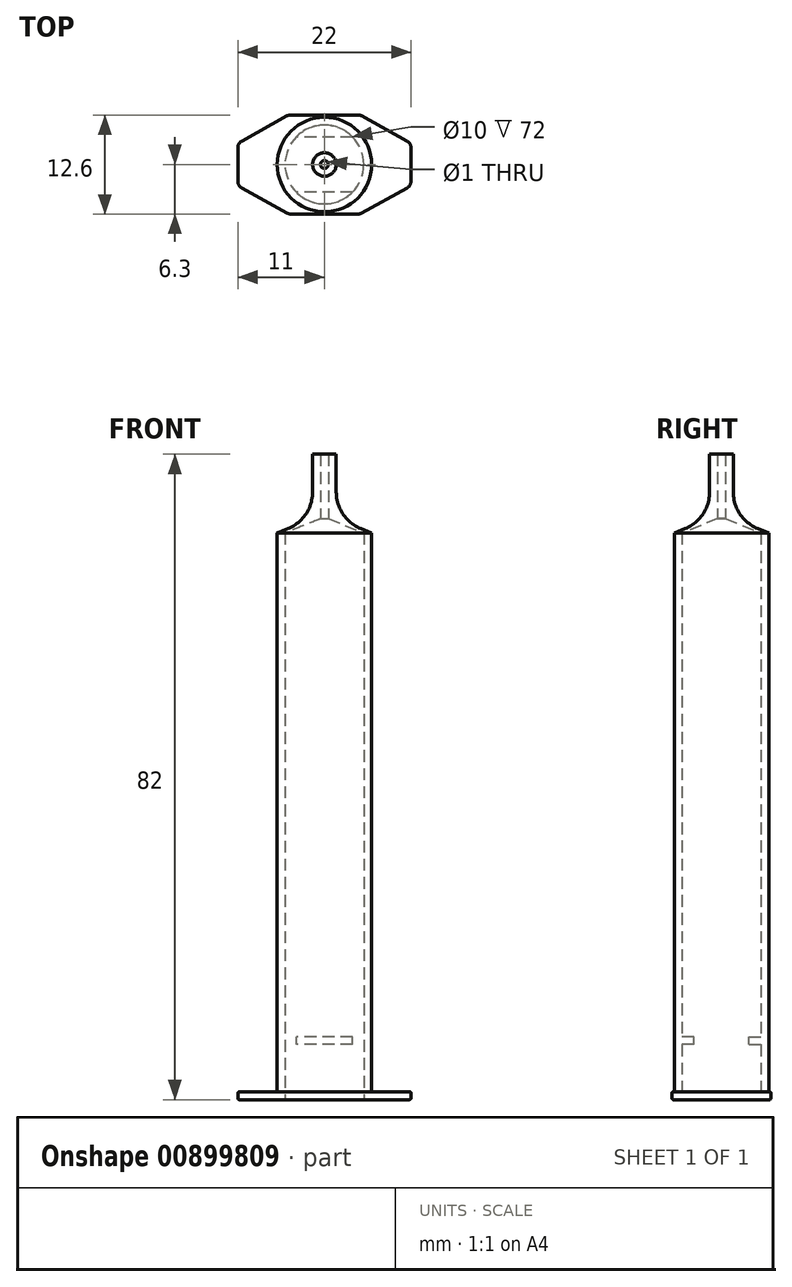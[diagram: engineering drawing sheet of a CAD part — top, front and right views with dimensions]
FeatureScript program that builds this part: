
annotation { "Feature Type Name" : "Feature", "Feature Type Description" : "" }
export const myFeature = defineFeature(function(context is Context, id is Id, definition is map)
    precondition{}
    {
        {
            var Q0;
            Q0=qCreatedBy(makeId("Top.planeOp"),FACE);
            var sketch = newSketch(context, id + "F0", { "sketchPlane" : qUnion([Q0])});
            skCircle(sketch, "E0", {"center": v(0, 0) * mm, "radius": 5 * mm});
            skCircle(sketch, "E1", {"center": v(0, 0) * mm, "radius": 6 * mm});
            skSolve(sketch);
        }
        {
            var Q0;
            Q0=makeQuery(id+"F0.imprint","IMPRINT",FACE,{"disambiguationData":[TD([[makeQuery(id+"F0.imprint","IMPRINT",EDGE,{"derivedFrom":sQuery(id+"F0.wireOp",EDGE,"E0")}),-1.0]])]});
            extrude(context, id + "F1", {"entities" : qUnion([Q0]), "depth" : 62 * mm, "offsetDistance" : 25 * mm, "hasSecondDirection" : true, "secondDirectionOppositeDirection" : true, "secondDirectionDepth" : 9 * mm});
        }
        {
            var Q0;
            Q0=qCreatedBy(makeId("Front.planeOp"),FACE);
            var sketch = newSketch(context, id + "F2", { "sketchPlane" : qUnion([Q0])});
            skLineSegment(sketch, "E2", {"start": v(4.64, 62.54) * mm, "end": v(6, 62) * mm});
            skLineSegment(sketch, "E3", {"start": v(0, 62) * mm, "end": v(6, 62) * mm});
            skLineSegment(sketch, "E4", {"start": v(0.5, 63.8) * mm, "end": v(5, 62) * mm});
            skLineSegment(sketch, "E5", {"start": v(0.5, 63.8) * mm, "end": v(0.5, 72) * mm});
            skLineSegment(sketch, "E6", {"start": v(1.5, 67.19) * mm, "end": v(1.5, 72) * mm});
            skLineSegment(sketch, "E7", {"start": v(0.5, 72) * mm, "end": v(1.5, 72) * mm});
            skLineSegment(sketch, "E8", {"start": v(0, 62) * mm, "end": v(0, 62.89) * mm});
            skPoint(sketch, "E9.visualSharp", {"position": v(1.5, 63.8) * mm});
            skArc(sketch, "E9.filletArc", {"start": v(1.5, 67.19) * mm, "mid": v(2.36, 64.38) * mm, "end": v(4.64, 62.54) * mm});
            skSolve(sketch);
        }
        {
            var Q0;
            {var subQ2=sQuery(id+"F2.wireOp",EDGE,"E2");Q0=makeQuery(id+"F2.imprint","IMPRINT",FACE,{"disambiguationData":[TD([[makeQuery(id+"F2.imprint","IMPRINT",EDGE,{"derivedFrom":subQ2}),-1.0]])]});}
            var Q1;
            Q1=sQuery(id+"F2.wireOp",EDGE,"E8");
            revolve(context, id + "F3", {"operationType" : NewBodyOperationType.ADD, "surfaceOperationType" : NewSurfaceOperationType.NEW, "entities" : qUnion([Q0]), "axis" : qUnion([Q1]), "revolveType" : RevolveType.FULL});
        }
        {
            var Q0;
            Q0=makeQuery(id+"F3.opRevolve","SWEPT_FACE",FACE,{"disambiguationData":[OSD([sQuery(id+"F2.wireOp",EDGE,"E7")])]});
            cPlane(context, id + "F4", {"entities" : qUnion([Q0]), "cplaneType" : CPlaneType.OFFSET, "offset" : 74 * mm, "oppositeDirection" : true, "width" : 150 * mm, "height" : 150 * mm});
        }
        {
            var Q0;
            Q0=qCreatedBy(id+"F4.planeOp",FACE);
            var sketch = newSketch(context, id + "F5", { "sketchPlane" : qUnion([Q0])});
            skLineSegment(sketch, "E10", {"start": v(3.57, 3.5) * mm, "end": v(-3.57, 3.5) * mm});
            skLineSegment(sketch, "E11.MirrorCS", {"start": v(3.57, -3.5) * mm, "end": v(-3.57, -3.5) * mm});
            skArc(sketch, "E12", {"start": v(-3.57, -3.5) * mm, "mid": v(0, -5) * mm, "end": v(3.57, -3.5) * mm});
            skArc(sketch, "E13.MirrorCS", {"start": v(-3.57, 3.5) * mm, "mid": v(0, 5) * mm, "end": v(3.57, 3.5) * mm});
            skSolve(sketch);
        }
        {
            var Q0;
            Q0=makeQuery(id+"F5.imprint","IMPRINT",FACE,{"disambiguationData":[TD([[makeQuery(id+"F5.imprint","IMPRINT",EDGE,{"derivedFrom":sQuery(id+"F5.wireOp",EDGE,"E11.MirrorCS")}),1.0]])]});
            var Q1;
            Q1=makeQuery(id+"F5.imprint","IMPRINT",FACE,{"disambiguationData":[TD([[makeQuery(id+"F5.imprint","IMPRINT",EDGE,{"derivedFrom":sQuery(id+"F5.wireOp",EDGE,"E10")}),-1.0]])]});
            extrude(context, id + "F6", {"entities" : qUnion([Q0, Q1]), "operationType" : NewBodyOperationType.ADD, "oppositeDirection" : true, "depth" : 1 * mm, "offsetDistance" : 25 * mm});
        }
        {
            var Q0;
            Q0=makeQuery(id+"F1.opExtrude","CAP_FACE",FACE,{"disambiguationData":[OSD([sQuery(id+"F0.wireOp",EDGE,"E0"),sQuery(id+"F0.wireOp",EDGE,"E1")])],"isStart":true});
            cPlane(context, id + "F7", {"entities" : qUnion([Q0]), "cplaneType" : CPlaneType.OFFSET, "offset" : 0 * mm, "width" : 150 * mm, "height" : 150 * mm});
        }
        {
            var Q0;
            Q0=qCreatedBy(id+"F7.planeOp",FACE);
            var sketch = newSketch(context, id + "F8", { "sketchPlane" : qUnion([Q0])});
            skLineSegment(sketch, "E14", {"start": v(4.5, 6.3) * mm, "end": v(11, 2.71) * mm});
            skLineSegment(sketch, "E15.MirrorCS", {"start": v(4.5, -6.3) * mm, "end": v(11, -2.71) * mm});
            skLineSegment(sketch, "E16.MirrorCS", {"start": v(-4.5, 6.3) * mm, "end": v(-11, 2.71) * mm});
            skLineSegment(sketch, "E17.MirrorCS", {"start": v(-4.5, -6.3) * mm, "end": v(-11, -2.71) * mm});
            skCircle(sketch, "E18", {"center": v(0, 0) * mm, "radius": 5 * mm});
            skLineSegment(sketch, "E19", {"start": v(4.5, 6.3) * mm, "end": v(-4.5, 6.3) * mm});
            skLineSegment(sketch, "E20", {"start": v(4.5, -6.3) * mm, "end": v(-4.5, -6.3) * mm});
            skLineSegment(sketch, "E21", {"start": v(11, 2.71) * mm, "end": v(11, -2.71) * mm});
            skLineSegment(sketch, "E22", {"start": v(-11, 2.71) * mm, "end": v(-11, -2.71) * mm});
            skSolve(sketch);
        }
        {
            var Q0;
            Q0=makeQuery(id+"F8.imprint","IMPRINT",FACE,{"disambiguationData":[TD([[makeQuery(id+"F8.imprint","IMPRINT",EDGE,{"derivedFrom":sQuery(id+"F8.wireOp",EDGE,"Z6K4M87V-DVPl-VIz8-pgWM-HxpkCWdUFoVx.top")}),1.0]])]});
            var Q1;
            Q1=makeQuery(id+"F8.imprint","IMPRINT",FACE,{"disambiguationData":[TD([[makeQuery(id+"F8.imprint","IMPRINT",EDGE,{"derivedFrom":sQuery(id+"F8.wireOp",EDGE,"E14")}),-1.0]])]});
            extrude(context, id + "F9", {"entities" : qUnion([Q0, Q1]), "operationType" : NewBodyOperationType.ADD, "depth" : 1 * mm, "offsetDistance" : 25 * mm});
        }
        {
            var Q0;
            Q0=makeQuery(id+"F9.opExtrude","SWEPT_EDGE",EDGE,{"disambiguationData":[OSD([sQuery(id+"F8.wireOp",EDGE,"df01a680-1bff-42a6-ba12-da2397d9a9860.MirrorCS"),sQuery(id+"F8.wireOp",EDGE,"E16.MirrorCS")])]});
            var Q1;
            Q1=makeQuery(id+"F9.opExtrude","SWEPT_EDGE",EDGE,{"disambiguationData":[OSD([sQuery(id+"F8.wireOp",EDGE,"07e45aba-89c8-4687-9971-865d9c13b24f0.MirrorCS"),sQuery(id+"F8.wireOp",EDGE,"E17.MirrorCS")])]});
            var Q2;
            Q2=makeQuery(id+"F9.opExtrude","SWEPT_EDGE",EDGE,{"disambiguationData":[OSD([sQuery(id+"F8.wireOp",EDGE,"Z6K4M87V-DVPl-VIz8-pgWM-HxpkCWdUFoVx.right"),sQuery(id+"F8.wireOp",EDGE,"E15.MirrorCS")])]});
            var Q3;
            Q3=makeQuery(id+"F9.opExtrude","SWEPT_EDGE",EDGE,{"disambiguationData":[OSD([sQuery(id+"F8.wireOp",EDGE,"6886a79b-2828-4634-8f31-eee592987a7b0.MirrorCS"),sQuery(id+"F8.wireOp",EDGE,"E14")])]});
            fillet(context, id + "F10", {"entities" : qUnion([Q0, Q1, Q2, Q3]), "radius" : 1 * mm, "tangentPropagation" : true, "allowEdgeOverflow" : false});
        }
        {
            var Q0;
            Q0=makeQuery(id+"F9.opExtrude","CAP_EDGE",EDGE,{"disambiguationData":[OSD([sQuery(id+"F8.wireOp",EDGE,"E16.MirrorCS")])],"isStart":false});
            var Q1;
            {var subQ0=sQuery(id+"F8.wireOp",EDGE,"E19");var subQ1=sQuery(id+"F8.wireOp",EDGE,"E16.MirrorCS");Q1=makeQuery(id+"F10.opFillet","BLEND_EDGE",EDGE,{"blendedFrom":[makeQuery(id+"F9.opExtrude","SWEPT_EDGE",EDGE,{"disambiguationData":[OSD([subQ1,subQ0])]}),makeQuery(id+"F9.opExtrude","CAP_FACE",FACE,{"disambiguationData":[OSD([sQuery(id+"F8.wireOp",EDGE,"E14"),sQuery(id+"F8.wireOp",EDGE,"E15.MirrorCS"),subQ1,sQuery(id+"F8.wireOp",EDGE,"E17.MirrorCS"),sQuery(id+"F8.wireOp",EDGE,"E18"),subQ0,sQuery(id+"F8.wireOp",EDGE,"E20"),sQuery(id+"F8.wireOp",EDGE,"E21"),sQuery(id+"F8.wireOp",EDGE,"E22")])],"isStart":false})],"blendedInto":[makeQuery(id+"F9.opExtrude","CAP_FACE",FACE,{"disambiguationData":[OSD([sQuery(id+"F8.wireOp",EDGE,"E14"),sQuery(id+"F8.wireOp",EDGE,"E15.MirrorCS"),subQ1,sQuery(id+"F8.wireOp",EDGE,"E17.MirrorCS"),sQuery(id+"F8.wireOp",EDGE,"E18"),subQ0,sQuery(id+"F8.wireOp",EDGE,"E20"),sQuery(id+"F8.wireOp",EDGE,"E21"),sQuery(id+"F8.wireOp",EDGE,"E22")])],"isStart":false})]});}
            var Q2;
            Q2=makeQuery(id+"F9.opExtrude","CAP_EDGE",EDGE,{"disambiguationData":[OSD([sQuery(id+"F8.wireOp",EDGE,"E19")])],"isStart":false});
            var Q3;
            Q3=makeQuery(id+"F9.opExtrude","CAP_EDGE",EDGE,{"disambiguationData":[OSD([sQuery(id+"F8.wireOp",EDGE,"E22")])],"isStart":false});
            var Q4;
            {var subQ0=sQuery(id+"F8.wireOp",EDGE,"E22");var subQ1=sQuery(id+"F8.wireOp",EDGE,"E16.MirrorCS");Q4=makeQuery(id+"F10.opFillet","BLEND_EDGE",EDGE,{"blendedFrom":[makeQuery(id+"F9.opExtrude","SWEPT_EDGE",EDGE,{"disambiguationData":[OSD([subQ1,subQ0])]}),makeQuery(id+"F9.opExtrude","CAP_FACE",FACE,{"disambiguationData":[OSD([sQuery(id+"F8.wireOp",EDGE,"E14"),sQuery(id+"F8.wireOp",EDGE,"E15.MirrorCS"),subQ1,sQuery(id+"F8.wireOp",EDGE,"E17.MirrorCS"),sQuery(id+"F8.wireOp",EDGE,"E18"),sQuery(id+"F8.wireOp",EDGE,"E19"),sQuery(id+"F8.wireOp",EDGE,"E20"),sQuery(id+"F8.wireOp",EDGE,"E21"),subQ0])],"isStart":false})],"blendedInto":[makeQuery(id+"F9.opExtrude","CAP_FACE",FACE,{"disambiguationData":[OSD([sQuery(id+"F8.wireOp",EDGE,"E14"),sQuery(id+"F8.wireOp",EDGE,"E15.MirrorCS"),subQ1,sQuery(id+"F8.wireOp",EDGE,"E17.MirrorCS"),sQuery(id+"F8.wireOp",EDGE,"E18"),sQuery(id+"F8.wireOp",EDGE,"E19"),sQuery(id+"F8.wireOp",EDGE,"E20"),sQuery(id+"F8.wireOp",EDGE,"E21"),subQ0])],"isStart":false})]});}
            var Q5;
            {var subQ0=sQuery(id+"F8.wireOp",EDGE,"E22");var subQ1=sQuery(id+"F8.wireOp",EDGE,"E17.MirrorCS");Q5=makeQuery(id+"F10.opFillet","BLEND_EDGE",EDGE,{"blendedFrom":[makeQuery(id+"F9.opExtrude","SWEPT_EDGE",EDGE,{"disambiguationData":[OSD([subQ1,subQ0])]}),makeQuery(id+"F9.opExtrude","CAP_FACE",FACE,{"disambiguationData":[OSD([sQuery(id+"F8.wireOp",EDGE,"E14"),sQuery(id+"F8.wireOp",EDGE,"E15.MirrorCS"),sQuery(id+"F8.wireOp",EDGE,"E16.MirrorCS"),subQ1,sQuery(id+"F8.wireOp",EDGE,"E18"),sQuery(id+"F8.wireOp",EDGE,"E19"),sQuery(id+"F8.wireOp",EDGE,"E20"),sQuery(id+"F8.wireOp",EDGE,"E21"),subQ0])],"isStart":false})],"blendedInto":[makeQuery(id+"F9.opExtrude","CAP_FACE",FACE,{"disambiguationData":[OSD([sQuery(id+"F8.wireOp",EDGE,"E14"),sQuery(id+"F8.wireOp",EDGE,"E15.MirrorCS"),sQuery(id+"F8.wireOp",EDGE,"E16.MirrorCS"),subQ1,sQuery(id+"F8.wireOp",EDGE,"E18"),sQuery(id+"F8.wireOp",EDGE,"E19"),sQuery(id+"F8.wireOp",EDGE,"E20"),sQuery(id+"F8.wireOp",EDGE,"E21"),subQ0])],"isStart":false})]});}
            var Q6;
            Q6=makeQuery(id+"F9.opExtrude","CAP_EDGE",EDGE,{"disambiguationData":[OSD([sQuery(id+"F8.wireOp",EDGE,"E17.MirrorCS")])],"isStart":false});
            var Q7;
            {var subQ0=sQuery(id+"F8.wireOp",EDGE,"E20");var subQ1=sQuery(id+"F8.wireOp",EDGE,"E17.MirrorCS");Q7=makeQuery(id+"F10.opFillet","BLEND_EDGE",EDGE,{"blendedFrom":[makeQuery(id+"F9.opExtrude","SWEPT_EDGE",EDGE,{"disambiguationData":[OSD([subQ1,subQ0])]}),makeQuery(id+"F9.opExtrude","CAP_FACE",FACE,{"disambiguationData":[OSD([sQuery(id+"F8.wireOp",EDGE,"E14"),sQuery(id+"F8.wireOp",EDGE,"E15.MirrorCS"),sQuery(id+"F8.wireOp",EDGE,"E16.MirrorCS"),subQ1,sQuery(id+"F8.wireOp",EDGE,"E18"),sQuery(id+"F8.wireOp",EDGE,"E19"),subQ0,sQuery(id+"F8.wireOp",EDGE,"E21"),sQuery(id+"F8.wireOp",EDGE,"E22")])],"isStart":false})],"blendedInto":[makeQuery(id+"F9.opExtrude","CAP_FACE",FACE,{"disambiguationData":[OSD([sQuery(id+"F8.wireOp",EDGE,"E14"),sQuery(id+"F8.wireOp",EDGE,"E15.MirrorCS"),sQuery(id+"F8.wireOp",EDGE,"E16.MirrorCS"),subQ1,sQuery(id+"F8.wireOp",EDGE,"E18"),sQuery(id+"F8.wireOp",EDGE,"E19"),subQ0,sQuery(id+"F8.wireOp",EDGE,"E21"),sQuery(id+"F8.wireOp",EDGE,"E22")])],"isStart":false})]});}
            var Q8;
            Q8=makeQuery(id+"F9.opExtrude","CAP_EDGE",EDGE,{"disambiguationData":[OSD([sQuery(id+"F8.wireOp",EDGE,"E20")])],"isStart":false});
            var Q9;
            {var subQ0=sQuery(id+"F8.wireOp",EDGE,"E20");var subQ1=sQuery(id+"F8.wireOp",EDGE,"E15.MirrorCS");Q9=makeQuery(id+"F10.opFillet","BLEND_EDGE",EDGE,{"blendedFrom":[makeQuery(id+"F9.opExtrude","SWEPT_EDGE",EDGE,{"disambiguationData":[OSD([subQ1,subQ0])]}),makeQuery(id+"F9.opExtrude","CAP_FACE",FACE,{"disambiguationData":[OSD([sQuery(id+"F8.wireOp",EDGE,"E14"),subQ1,sQuery(id+"F8.wireOp",EDGE,"E16.MirrorCS"),sQuery(id+"F8.wireOp",EDGE,"E17.MirrorCS"),sQuery(id+"F8.wireOp",EDGE,"E18"),sQuery(id+"F8.wireOp",EDGE,"E19"),subQ0,sQuery(id+"F8.wireOp",EDGE,"E21"),sQuery(id+"F8.wireOp",EDGE,"E22")])],"isStart":false})],"blendedInto":[makeQuery(id+"F9.opExtrude","CAP_FACE",FACE,{"disambiguationData":[OSD([sQuery(id+"F8.wireOp",EDGE,"E14"),subQ1,sQuery(id+"F8.wireOp",EDGE,"E16.MirrorCS"),sQuery(id+"F8.wireOp",EDGE,"E17.MirrorCS"),sQuery(id+"F8.wireOp",EDGE,"E18"),sQuery(id+"F8.wireOp",EDGE,"E19"),subQ0,sQuery(id+"F8.wireOp",EDGE,"E21"),sQuery(id+"F8.wireOp",EDGE,"E22")])],"isStart":false})]});}
            var Q10;
            Q10=makeQuery(id+"F9.opExtrude","CAP_EDGE",EDGE,{"disambiguationData":[OSD([sQuery(id+"F8.wireOp",EDGE,"E15.MirrorCS")])],"isStart":false});
            var Q11;
            Q11=makeQuery(id+"F9.opExtrude","CAP_EDGE",EDGE,{"disambiguationData":[OSD([sQuery(id+"F8.wireOp",EDGE,"E14")])],"isStart":false});
            var Q12;
            {var subQ0=sQuery(id+"F8.wireOp",EDGE,"E19");var subQ1=sQuery(id+"F8.wireOp",EDGE,"E14");Q12=makeQuery(id+"F10.opFillet","BLEND_EDGE",EDGE,{"blendedFrom":[makeQuery(id+"F9.opExtrude","SWEPT_EDGE",EDGE,{"disambiguationData":[OSD([subQ1,subQ0])]}),makeQuery(id+"F9.opExtrude","CAP_FACE",FACE,{"disambiguationData":[OSD([subQ1,sQuery(id+"F8.wireOp",EDGE,"E15.MirrorCS"),sQuery(id+"F8.wireOp",EDGE,"E16.MirrorCS"),sQuery(id+"F8.wireOp",EDGE,"E17.MirrorCS"),sQuery(id+"F8.wireOp",EDGE,"E18"),subQ0,sQuery(id+"F8.wireOp",EDGE,"E20"),sQuery(id+"F8.wireOp",EDGE,"E21"),sQuery(id+"F8.wireOp",EDGE,"E22")])],"isStart":false})],"blendedInto":[makeQuery(id+"F9.opExtrude","CAP_FACE",FACE,{"disambiguationData":[OSD([subQ1,sQuery(id+"F8.wireOp",EDGE,"E15.MirrorCS"),sQuery(id+"F8.wireOp",EDGE,"E16.MirrorCS"),sQuery(id+"F8.wireOp",EDGE,"E17.MirrorCS"),sQuery(id+"F8.wireOp",EDGE,"E18"),subQ0,sQuery(id+"F8.wireOp",EDGE,"E20"),sQuery(id+"F8.wireOp",EDGE,"E21"),sQuery(id+"F8.wireOp",EDGE,"E22")])],"isStart":false})]});}
            var Q13;
            {var subQ0=sQuery(id+"F8.wireOp",EDGE,"E21");var subQ1=sQuery(id+"F8.wireOp",EDGE,"E14");Q13=makeQuery(id+"F10.opFillet","BLEND_EDGE",EDGE,{"blendedFrom":[makeQuery(id+"F9.opExtrude","SWEPT_EDGE",EDGE,{"disambiguationData":[OSD([subQ1,subQ0])]}),makeQuery(id+"F9.opExtrude","CAP_FACE",FACE,{"disambiguationData":[OSD([subQ1,sQuery(id+"F8.wireOp",EDGE,"E15.MirrorCS"),sQuery(id+"F8.wireOp",EDGE,"E16.MirrorCS"),sQuery(id+"F8.wireOp",EDGE,"E17.MirrorCS"),sQuery(id+"F8.wireOp",EDGE,"E18"),sQuery(id+"F8.wireOp",EDGE,"E19"),sQuery(id+"F8.wireOp",EDGE,"E20"),subQ0,sQuery(id+"F8.wireOp",EDGE,"E22")])],"isStart":false})],"blendedInto":[makeQuery(id+"F9.opExtrude","CAP_FACE",FACE,{"disambiguationData":[OSD([subQ1,sQuery(id+"F8.wireOp",EDGE,"E15.MirrorCS"),sQuery(id+"F8.wireOp",EDGE,"E16.MirrorCS"),sQuery(id+"F8.wireOp",EDGE,"E17.MirrorCS"),sQuery(id+"F8.wireOp",EDGE,"E18"),sQuery(id+"F8.wireOp",EDGE,"E19"),sQuery(id+"F8.wireOp",EDGE,"E20"),subQ0,sQuery(id+"F8.wireOp",EDGE,"E22")])],"isStart":false})]});}
            var Q14;
            Q14=makeQuery(id+"F9.opExtrude","CAP_EDGE",EDGE,{"disambiguationData":[OSD([sQuery(id+"F8.wireOp",EDGE,"E21")])],"isStart":false});
            var Q15;
            {var subQ0=sQuery(id+"F8.wireOp",EDGE,"E21");var subQ1=sQuery(id+"F8.wireOp",EDGE,"E15.MirrorCS");Q15=makeQuery(id+"F10.opFillet","BLEND_EDGE",EDGE,{"blendedFrom":[makeQuery(id+"F9.opExtrude","SWEPT_EDGE",EDGE,{"disambiguationData":[OSD([subQ1,subQ0])]}),makeQuery(id+"F9.opExtrude","CAP_FACE",FACE,{"disambiguationData":[OSD([sQuery(id+"F8.wireOp",EDGE,"E14"),subQ1,sQuery(id+"F8.wireOp",EDGE,"E16.MirrorCS"),sQuery(id+"F8.wireOp",EDGE,"E17.MirrorCS"),sQuery(id+"F8.wireOp",EDGE,"E18"),sQuery(id+"F8.wireOp",EDGE,"E19"),sQuery(id+"F8.wireOp",EDGE,"E20"),subQ0,sQuery(id+"F8.wireOp",EDGE,"E22")])],"isStart":false})],"blendedInto":[makeQuery(id+"F9.opExtrude","CAP_FACE",FACE,{"disambiguationData":[OSD([sQuery(id+"F8.wireOp",EDGE,"E14"),subQ1,sQuery(id+"F8.wireOp",EDGE,"E16.MirrorCS"),sQuery(id+"F8.wireOp",EDGE,"E17.MirrorCS"),sQuery(id+"F8.wireOp",EDGE,"E18"),sQuery(id+"F8.wireOp",EDGE,"E19"),sQuery(id+"F8.wireOp",EDGE,"E20"),subQ0,sQuery(id+"F8.wireOp",EDGE,"E22")])],"isStart":false})]});}
            fillet(context, id + "F11", {"entities" : qUnion([Q0, Q1, Q2, Q3, Q4, Q5, Q6, Q7, Q8, Q9, Q10, Q11, Q12, Q13, Q14, Q15]), "radius" : .2 * mm, "tangentPropagation" : true, "allowEdgeOverflow" : false});
        }
        {
            var Q0;
            {var subQ0=sQuery(id+"F8.wireOp",EDGE,"E21");var subQ1=sQuery(id+"F8.wireOp",EDGE,"E14");Q0=makeQuery(id+"F10.opFillet","BLEND_EDGE",EDGE,{"blendedFrom":[makeQuery(id+"F9.opExtrude","SWEPT_EDGE",EDGE,{"disambiguationData":[OSD([subQ1,subQ0])]}),makeQuery(id+"F9.opExtrude","CAP_FACE",FACE,{"disambiguationData":[OSD([subQ1,sQuery(id+"F8.wireOp",EDGE,"E15.MirrorCS"),sQuery(id+"F8.wireOp",EDGE,"E16.MirrorCS"),sQuery(id+"F8.wireOp",EDGE,"E17.MirrorCS"),sQuery(id+"F8.wireOp",EDGE,"E18"),sQuery(id+"F8.wireOp",EDGE,"E19"),sQuery(id+"F8.wireOp",EDGE,"E20"),subQ0,sQuery(id+"F8.wireOp",EDGE,"E22")])],"isStart":true})],"blendedInto":[makeQuery(id+"F9.opExtrude","CAP_FACE",FACE,{"disambiguationData":[OSD([subQ1,sQuery(id+"F8.wireOp",EDGE,"E15.MirrorCS"),sQuery(id+"F8.wireOp",EDGE,"E16.MirrorCS"),sQuery(id+"F8.wireOp",EDGE,"E17.MirrorCS"),sQuery(id+"F8.wireOp",EDGE,"E18"),sQuery(id+"F8.wireOp",EDGE,"E19"),sQuery(id+"F8.wireOp",EDGE,"E20"),subQ0,sQuery(id+"F8.wireOp",EDGE,"E22")])],"isStart":true})]});}
            var Q1;
            Q1=makeQuery(id+"F9.opExtrude","CAP_EDGE",EDGE,{"disambiguationData":[OSD([sQuery(id+"F8.wireOp",EDGE,"E21")])],"isStart":true});
            var Q2;
            {var subQ0=sQuery(id+"F8.wireOp",EDGE,"E21");var subQ1=sQuery(id+"F8.wireOp",EDGE,"E15.MirrorCS");Q2=makeQuery(id+"F10.opFillet","BLEND_EDGE",EDGE,{"blendedFrom":[makeQuery(id+"F9.opExtrude","SWEPT_EDGE",EDGE,{"disambiguationData":[OSD([subQ1,subQ0])]}),makeQuery(id+"F9.opExtrude","CAP_FACE",FACE,{"disambiguationData":[OSD([sQuery(id+"F8.wireOp",EDGE,"E14"),subQ1,sQuery(id+"F8.wireOp",EDGE,"E16.MirrorCS"),sQuery(id+"F8.wireOp",EDGE,"E17.MirrorCS"),sQuery(id+"F8.wireOp",EDGE,"E18"),sQuery(id+"F8.wireOp",EDGE,"E19"),sQuery(id+"F8.wireOp",EDGE,"E20"),subQ0,sQuery(id+"F8.wireOp",EDGE,"E22")])],"isStart":true})],"blendedInto":[makeQuery(id+"F9.opExtrude","CAP_FACE",FACE,{"disambiguationData":[OSD([sQuery(id+"F8.wireOp",EDGE,"E14"),subQ1,sQuery(id+"F8.wireOp",EDGE,"E16.MirrorCS"),sQuery(id+"F8.wireOp",EDGE,"E17.MirrorCS"),sQuery(id+"F8.wireOp",EDGE,"E18"),sQuery(id+"F8.wireOp",EDGE,"E19"),sQuery(id+"F8.wireOp",EDGE,"E20"),subQ0,sQuery(id+"F8.wireOp",EDGE,"E22")])],"isStart":true})]});}
            var Q3;
            Q3=makeQuery(id+"F9.opExtrude","CAP_EDGE",EDGE,{"disambiguationData":[OSD([sQuery(id+"F8.wireOp",EDGE,"E15.MirrorCS")])],"isStart":true});
            var Q4;
            {var subQ0=sQuery(id+"F8.wireOp",EDGE,"E20");var subQ1=sQuery(id+"F8.wireOp",EDGE,"E15.MirrorCS");Q4=makeQuery(id+"F10.opFillet","BLEND_EDGE",EDGE,{"blendedFrom":[makeQuery(id+"F9.opExtrude","SWEPT_EDGE",EDGE,{"disambiguationData":[OSD([subQ1,subQ0])]}),makeQuery(id+"F9.opExtrude","CAP_FACE",FACE,{"disambiguationData":[OSD([sQuery(id+"F8.wireOp",EDGE,"E14"),subQ1,sQuery(id+"F8.wireOp",EDGE,"E16.MirrorCS"),sQuery(id+"F8.wireOp",EDGE,"E17.MirrorCS"),sQuery(id+"F8.wireOp",EDGE,"E18"),sQuery(id+"F8.wireOp",EDGE,"E19"),subQ0,sQuery(id+"F8.wireOp",EDGE,"E21"),sQuery(id+"F8.wireOp",EDGE,"E22")])],"isStart":true})],"blendedInto":[makeQuery(id+"F9.opExtrude","CAP_FACE",FACE,{"disambiguationData":[OSD([sQuery(id+"F8.wireOp",EDGE,"E14"),subQ1,sQuery(id+"F8.wireOp",EDGE,"E16.MirrorCS"),sQuery(id+"F8.wireOp",EDGE,"E17.MirrorCS"),sQuery(id+"F8.wireOp",EDGE,"E18"),sQuery(id+"F8.wireOp",EDGE,"E19"),subQ0,sQuery(id+"F8.wireOp",EDGE,"E21"),sQuery(id+"F8.wireOp",EDGE,"E22")])],"isStart":true})]});}
            var Q5;
            Q5=makeQuery(id+"F9.opExtrude","CAP_EDGE",EDGE,{"disambiguationData":[OSD([sQuery(id+"F8.wireOp",EDGE,"E20")])],"isStart":true});
            var Q6;
            {var subQ0=sQuery(id+"F8.wireOp",EDGE,"E20");var subQ1=sQuery(id+"F8.wireOp",EDGE,"E17.MirrorCS");Q6=makeQuery(id+"F10.opFillet","BLEND_EDGE",EDGE,{"blendedFrom":[makeQuery(id+"F9.opExtrude","SWEPT_EDGE",EDGE,{"disambiguationData":[OSD([subQ1,subQ0])]}),makeQuery(id+"F9.opExtrude","CAP_FACE",FACE,{"disambiguationData":[OSD([sQuery(id+"F8.wireOp",EDGE,"E14"),sQuery(id+"F8.wireOp",EDGE,"E15.MirrorCS"),sQuery(id+"F8.wireOp",EDGE,"E16.MirrorCS"),subQ1,sQuery(id+"F8.wireOp",EDGE,"E18"),sQuery(id+"F8.wireOp",EDGE,"E19"),subQ0,sQuery(id+"F8.wireOp",EDGE,"E21"),sQuery(id+"F8.wireOp",EDGE,"E22")])],"isStart":true})],"blendedInto":[makeQuery(id+"F9.opExtrude","CAP_FACE",FACE,{"disambiguationData":[OSD([sQuery(id+"F8.wireOp",EDGE,"E14"),sQuery(id+"F8.wireOp",EDGE,"E15.MirrorCS"),sQuery(id+"F8.wireOp",EDGE,"E16.MirrorCS"),subQ1,sQuery(id+"F8.wireOp",EDGE,"E18"),sQuery(id+"F8.wireOp",EDGE,"E19"),subQ0,sQuery(id+"F8.wireOp",EDGE,"E21"),sQuery(id+"F8.wireOp",EDGE,"E22")])],"isStart":true})]});}
            var Q7;
            {var subQ0=sQuery(id+"F8.wireOp",EDGE,"E22");var subQ1=sQuery(id+"F8.wireOp",EDGE,"E17.MirrorCS");Q7=makeQuery(id+"F10.opFillet","BLEND_EDGE",EDGE,{"blendedFrom":[makeQuery(id+"F9.opExtrude","SWEPT_EDGE",EDGE,{"disambiguationData":[OSD([subQ1,subQ0])]}),makeQuery(id+"F9.opExtrude","CAP_FACE",FACE,{"disambiguationData":[OSD([sQuery(id+"F8.wireOp",EDGE,"E14"),sQuery(id+"F8.wireOp",EDGE,"E15.MirrorCS"),sQuery(id+"F8.wireOp",EDGE,"E16.MirrorCS"),subQ1,sQuery(id+"F8.wireOp",EDGE,"E18"),sQuery(id+"F8.wireOp",EDGE,"E19"),sQuery(id+"F8.wireOp",EDGE,"E20"),sQuery(id+"F8.wireOp",EDGE,"E21"),subQ0])],"isStart":true})],"blendedInto":[makeQuery(id+"F9.opExtrude","CAP_FACE",FACE,{"disambiguationData":[OSD([sQuery(id+"F8.wireOp",EDGE,"E14"),sQuery(id+"F8.wireOp",EDGE,"E15.MirrorCS"),sQuery(id+"F8.wireOp",EDGE,"E16.MirrorCS"),subQ1,sQuery(id+"F8.wireOp",EDGE,"E18"),sQuery(id+"F8.wireOp",EDGE,"E19"),sQuery(id+"F8.wireOp",EDGE,"E20"),sQuery(id+"F8.wireOp",EDGE,"E21"),subQ0])],"isStart":true})]});}
            var Q8;
            Q8=makeQuery(id+"F9.opExtrude","CAP_EDGE",EDGE,{"disambiguationData":[OSD([sQuery(id+"F8.wireOp",EDGE,"E17.MirrorCS")])],"isStart":true});
            var Q9;
            Q9=makeQuery(id+"F9.opExtrude","CAP_EDGE",EDGE,{"disambiguationData":[OSD([sQuery(id+"F8.wireOp",EDGE,"E14")])],"isStart":true});
            var Q10;
            Q10=makeQuery(id+"F9.opExtrude","CAP_EDGE",EDGE,{"disambiguationData":[OSD([sQuery(id+"F8.wireOp",EDGE,"E19")])],"isStart":true});
            var Q11;
            Q11=makeQuery(id+"F9.opExtrude","CAP_EDGE",EDGE,{"disambiguationData":[OSD([sQuery(id+"F8.wireOp",EDGE,"E22")])],"isStart":true});
            var Q12;
            {var subQ0=sQuery(id+"F8.wireOp",EDGE,"E22");var subQ1=sQuery(id+"F8.wireOp",EDGE,"E16.MirrorCS");Q12=makeQuery(id+"F10.opFillet","BLEND_EDGE",EDGE,{"blendedFrom":[makeQuery(id+"F9.opExtrude","SWEPT_EDGE",EDGE,{"disambiguationData":[OSD([subQ1,subQ0])]}),makeQuery(id+"F9.opExtrude","CAP_FACE",FACE,{"disambiguationData":[OSD([sQuery(id+"F8.wireOp",EDGE,"E14"),sQuery(id+"F8.wireOp",EDGE,"E15.MirrorCS"),subQ1,sQuery(id+"F8.wireOp",EDGE,"E17.MirrorCS"),sQuery(id+"F8.wireOp",EDGE,"E18"),sQuery(id+"F8.wireOp",EDGE,"E19"),sQuery(id+"F8.wireOp",EDGE,"E20"),sQuery(id+"F8.wireOp",EDGE,"E21"),subQ0])],"isStart":true})],"blendedInto":[makeQuery(id+"F9.opExtrude","CAP_FACE",FACE,{"disambiguationData":[OSD([sQuery(id+"F8.wireOp",EDGE,"E14"),sQuery(id+"F8.wireOp",EDGE,"E15.MirrorCS"),subQ1,sQuery(id+"F8.wireOp",EDGE,"E17.MirrorCS"),sQuery(id+"F8.wireOp",EDGE,"E18"),sQuery(id+"F8.wireOp",EDGE,"E19"),sQuery(id+"F8.wireOp",EDGE,"E20"),sQuery(id+"F8.wireOp",EDGE,"E21"),subQ0])],"isStart":true})]});}
            var Q13;
            {var subQ0=sQuery(id+"F8.wireOp",EDGE,"E19");var subQ1=sQuery(id+"F8.wireOp",EDGE,"E16.MirrorCS");Q13=makeQuery(id+"F10.opFillet","BLEND_EDGE",EDGE,{"blendedFrom":[makeQuery(id+"F9.opExtrude","SWEPT_EDGE",EDGE,{"disambiguationData":[OSD([subQ1,subQ0])]}),makeQuery(id+"F9.opExtrude","CAP_FACE",FACE,{"disambiguationData":[OSD([sQuery(id+"F8.wireOp",EDGE,"E14"),sQuery(id+"F8.wireOp",EDGE,"E15.MirrorCS"),subQ1,sQuery(id+"F8.wireOp",EDGE,"E17.MirrorCS"),sQuery(id+"F8.wireOp",EDGE,"E18"),subQ0,sQuery(id+"F8.wireOp",EDGE,"E20"),sQuery(id+"F8.wireOp",EDGE,"E21"),sQuery(id+"F8.wireOp",EDGE,"E22")])],"isStart":true})],"blendedInto":[makeQuery(id+"F9.opExtrude","CAP_FACE",FACE,{"disambiguationData":[OSD([sQuery(id+"F8.wireOp",EDGE,"E14"),sQuery(id+"F8.wireOp",EDGE,"E15.MirrorCS"),subQ1,sQuery(id+"F8.wireOp",EDGE,"E17.MirrorCS"),sQuery(id+"F8.wireOp",EDGE,"E18"),subQ0,sQuery(id+"F8.wireOp",EDGE,"E20"),sQuery(id+"F8.wireOp",EDGE,"E21"),sQuery(id+"F8.wireOp",EDGE,"E22")])],"isStart":true})]});}
            var Q14;
            {var subQ0=sQuery(id+"F8.wireOp",EDGE,"E19");var subQ1=sQuery(id+"F8.wireOp",EDGE,"E14");Q14=makeQuery(id+"F10.opFillet","BLEND_EDGE",EDGE,{"blendedFrom":[makeQuery(id+"F9.opExtrude","SWEPT_EDGE",EDGE,{"disambiguationData":[OSD([subQ1,subQ0])]}),makeQuery(id+"F9.opExtrude","CAP_FACE",FACE,{"disambiguationData":[OSD([subQ1,sQuery(id+"F8.wireOp",EDGE,"E15.MirrorCS"),sQuery(id+"F8.wireOp",EDGE,"E16.MirrorCS"),sQuery(id+"F8.wireOp",EDGE,"E17.MirrorCS"),sQuery(id+"F8.wireOp",EDGE,"E18"),subQ0,sQuery(id+"F8.wireOp",EDGE,"E20"),sQuery(id+"F8.wireOp",EDGE,"E21"),sQuery(id+"F8.wireOp",EDGE,"E22")])],"isStart":true})],"blendedInto":[makeQuery(id+"F9.opExtrude","CAP_FACE",FACE,{"disambiguationData":[OSD([subQ1,sQuery(id+"F8.wireOp",EDGE,"E15.MirrorCS"),sQuery(id+"F8.wireOp",EDGE,"E16.MirrorCS"),sQuery(id+"F8.wireOp",EDGE,"E17.MirrorCS"),sQuery(id+"F8.wireOp",EDGE,"E18"),subQ0,sQuery(id+"F8.wireOp",EDGE,"E20"),sQuery(id+"F8.wireOp",EDGE,"E21"),sQuery(id+"F8.wireOp",EDGE,"E22")])],"isStart":true})]});}
            var Q15;
            Q15=makeQuery(id+"F9.opExtrude","CAP_EDGE",EDGE,{"disambiguationData":[OSD([sQuery(id+"F8.wireOp",EDGE,"E16.MirrorCS")])],"isStart":true});
            fillet(context, id + "F12", {"entities" : qUnion([Q0, Q1, Q2, Q3, Q4, Q5, Q6, Q7, Q8, Q9, Q10, Q11, Q12, Q13, Q14, Q15]), "radius" : .2 * mm, "tangentPropagation" : true, "allowEdgeOverflow" : false});
        }
    });
